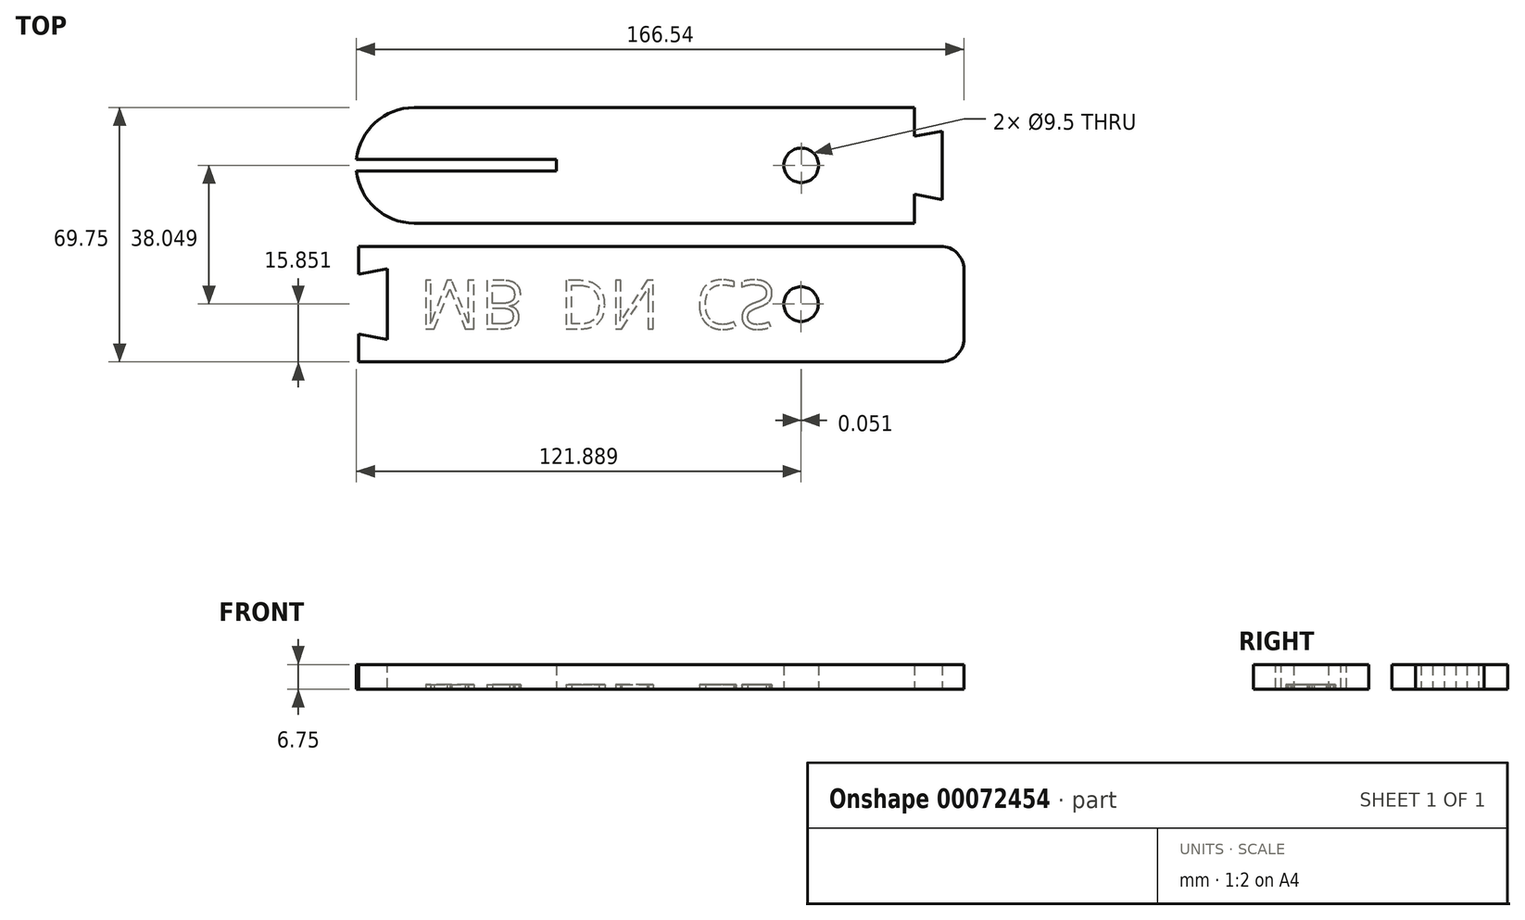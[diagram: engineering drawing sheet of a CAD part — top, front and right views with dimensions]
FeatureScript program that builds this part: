
annotation { "Feature Type Name" : "Feature", "Feature Type Description" : "" }
export const myFeature = defineFeature(function(context is Context, id is Id, definition is map)
    precondition{}
    {
        {
            var Q0;
            Q0=qCreatedBy(makeId("Top.planeOp"),FACE);
            var sketch = newSketch(context, id + "F0", { "sketchPlane" : qUnion([Q0])});
            skLineSegment(sketch, "E0", {"start": v(-148.8, 0) * mm, "end": v(170.22, 0) * mm});
            skLineSegment(sketch, "E1", {"start": v(28.97, 0) * mm, "end": v(28.97, 15.85) * mm});
            skLineSegment(sketch, "E2.MirrorCS", {"start": v(28.97, 0) * mm, "end": v(28.97, -15.85) * mm});
            skLineSegment(sketch, "E3.bottom", {"start": v(-132.95, 15.85) * mm, "end": v(163.87, 15.85) * mm});
            skLineSegment(sketch, "E3.top", {"start": v(-132.95, -15.85) * mm, "end": v(163.87, -15.85) * mm});
            skLineSegment(sketch, "E3.left", {"start": v(-148.8, 0) * mm, "end": v(-148.8, 0) * mm});
            skLineSegment(sketch, "E3.right", {"start": v(170.22, 9.5) * mm, "end": v(170.22, -9.5) * mm});
            skLineSegment(sketch, "E4", {"start": v(-157.4, 0) * mm, "end": v(-157.4, 1.59) * mm});
            skLineSegment(sketch, "E5", {"start": v(-148.8, 25.83) * mm, "end": v(-93.87, 25.83) * mm});
            skLineSegment(sketch, "E6", {"start": v(-148.8, 1.59) * mm, "end": v(-93.87, 1.59) * mm});
            skLineSegment(sketch, "E7.MirrorCS", {"start": v(-148.8, -1.59) * mm, "end": v(-93.87, -1.59) * mm});
            skLineSegment(sketch, "E8", {"start": v(-93.87, -1.59) * mm, "end": v(-93.87, 1.59) * mm});
            skPoint(sketch, "E9.visualSharp", {"position": v(-148.8, 15.85) * mm});
            skArc(sketch, "E9.filletArc", {"start": v(-132.95, 15.85) * mm, "mid": v(-144.16, 11.2) * mm, "end": v(-148.8, 0) * mm});
            skPoint(sketch, "E10.visualSharp", {"position": v(-148.8, -15.85) * mm});
            skArc(sketch, "E10.filletArc", {"start": v(-148.8, 0) * mm, "mid": v(-144.16, -11.2) * mm, "end": v(-132.95, -15.85) * mm});
            skLineSegment(sketch, "E11", {"start": v(170.22, -41.65) * mm, "end": v(125.57, -41.65) * mm});
            skLineSegment(sketch, "E12", {"start": v(170.22, -67.38) * mm, "end": v(-26.78, -67.38) * mm});
            skCircle(sketch, "E13", {"center": v(-26.78, 0) * mm, "radius": 4.75 * mm});
            skCircle(sketch, "E14", {"center": v(125.57, 0) * mm, "radius": 4.75 * mm});
            skLineSegment(sketch, "E15", {"start": v(4.2, 15.85) * mm, "end": v(4.2, 7.92) * mm});
            skPoint(sketch, "E15.endSnap0", {"position": v(28.97, 7.92) * mm});
            skLineSegment(sketch, "E16", {"start": v(4.2, 7.92) * mm, "end": v(11.86, 9.43) * mm});
            skLineSegment(sketch, "E17", {"start": v(11.86, 9.43) * mm, "end": v(11.86, 0) * mm});
            skLineSegment(sketch, "E18.MirrorCS", {"start": v(4.2, -7.92) * mm, "end": v(11.86, -9.43) * mm});
            skLineSegment(sketch, "E19.MirrorCS", {"start": v(11.86, -9.43) * mm, "end": v(11.86, 0) * mm});
            skLineSegment(sketch, "E20.MirrorCS", {"start": v(4.2, -15.85) * mm, "end": v(4.2, -7.92) * mm});
            skPoint(sketch, "E21.visualSharp", {"position": v(170.22, 15.85) * mm});
            skArc(sketch, "E21.filletArc", {"start": v(170.22, 9.5) * mm, "mid": v(168.36, 13.99) * mm, "end": v(163.87, 15.85) * mm});
            skPoint(sketch, "E22.visualSharp", {"position": v(170.22, -15.85) * mm});
            skArc(sketch, "E22.filletArc", {"start": v(163.87, -15.85) * mm, "mid": v(168.36, -13.99) * mm, "end": v(170.22, -9.5) * mm});
            skSolve(sketch);
        }
        {
            var Q0;
            {var subQ3=sQuery(id+"F0.wireOp",EDGE,"E15");Q0=makeQuery(id+"F0.imprint","IMPRINT",FACE,{"disambiguationData":[TD([[makeQuery(id+"F0.imprint","IMPRINT",EDGE,{"derivedFrom":subQ3}),-1.0]])]});}
            var Q1;
            Q1=makeQuery(id+"F0.imprint","IMPRINT",FACE,{"disambiguationData":[TD([[makeQuery(id+"F0.imprint","IMPRINT",EDGE,{"derivedFrom":sQuery(id+"F0.wireOp",EDGE,"E18.MirrorCS")}),1.0]])]});
            extrude(context, id + "F1", {"entities" : qUnion([Q0, Q1]), "depth" : 6.35 * mm});
        }
        {
            var Q0;
            {var subQ1=sQuery(id+"F0.wireOp",EDGE,"E2.MirrorCS");Q0=makeQuery(id+"F0.imprint","IMPRINT",FACE,{"disambiguationData":[TD([[makeQuery(id+"F0.imprint","IMPRINT",EDGE,{"derivedFrom":subQ1}),1.0]])]});}
            var Q1;
            {var subQ1=sQuery(id+"F0.wireOp",EDGE,"E1");Q1=makeQuery(id+"F0.imprint","IMPRINT",FACE,{"disambiguationData":[TD([[makeQuery(id+"F0.imprint","IMPRINT",EDGE,{"derivedFrom":subQ1}),-1.0]])]});}
            var Q2;
            {var subQ0=sQuery(id+"F0.wireOp",EDGE,"E2.MirrorCS");Q2=makeQuery(id+"F0.imprint","IMPRINT",FACE,{"disambiguationData":[TD([[makeQuery(id+"F0.imprint","IMPRINT",EDGE,{"derivedFrom":subQ0}),-1.0]])]});}
            var Q3;
            {var subQ2=sQuery(id+"F0.wireOp",EDGE,"E1");Q3=makeQuery(id+"F0.imprint","IMPRINT",FACE,{"disambiguationData":[TD([[makeQuery(id+"F0.imprint","IMPRINT",EDGE,{"derivedFrom":subQ2}),1.0]])]});}
            extrude(context, id + "F2", {"entities" : qUnion([Q0, Q1, Q2, Q3]), "depth" : 6.35 * mm});
        }
        {
            var Q0;
            Q0=makeQuery(id+"F2.opExtrude","SWEPT_BODY",BODY,{"disambiguationData":[OSD([sQuery(id+"F0.wireOp",EDGE,"E3.bottom"),sQuery(id+"F0.wireOp",EDGE,"E3.top"),sQuery(id+"F0.wireOp",EDGE,"E3.right"),sQuery(id+"F0.wireOp",EDGE,"E14"),sQuery(id+"F0.wireOp",EDGE,"E15"),sQuery(id+"F0.wireOp",EDGE,"E16"),sQuery(id+"F0.wireOp",EDGE,"E17"),sQuery(id+"F0.wireOp",EDGE,"E18.MirrorCS"),sQuery(id+"F0.wireOp",EDGE,"E19.MirrorCS"),sQuery(id+"F0.wireOp",EDGE,"E20.MirrorCS"),sQuery(id+"F0.wireOp",EDGE,"E21.filletArc"),sQuery(id+"F0.wireOp",EDGE,"E22.filletArc")])]});
            var Q1;
            Q1=sQuery(id+"F0.wireOp",EDGE,"E2.MirrorCS");
            transform(context, id + "F3", {"entities" : qUnion([Q0]), "transformType" : TransformType.TRANSLATION_ENTITY, "oppositeDirectionEntity" : false, "transformLine" : qUnion([Q1]), "makeCopy" : false});
        }
        {
            var Q0;
            Q0=makeQuery(id+"F2.opExtrude","SWEPT_BODY",BODY,{"disambiguationData":[OSD([sQuery(id+"F0.wireOp",EDGE,"E3.bottom"),sQuery(id+"F0.wireOp",EDGE,"E3.top"),sQuery(id+"F0.wireOp",EDGE,"E3.right"),sQuery(id+"F0.wireOp",EDGE,"E14"),sQuery(id+"F0.wireOp",EDGE,"E15"),sQuery(id+"F0.wireOp",EDGE,"E16"),sQuery(id+"F0.wireOp",EDGE,"E17"),sQuery(id+"F0.wireOp",EDGE,"E18.MirrorCS"),sQuery(id+"F0.wireOp",EDGE,"E19.MirrorCS"),sQuery(id+"F0.wireOp",EDGE,"E20.MirrorCS"),sQuery(id+"F0.wireOp",EDGE,"E21.filletArc"),sQuery(id+"F0.wireOp",EDGE,"E22.filletArc")])]});
            var Q1;
            Q1=sQuery(id+"F0.wireOp",EDGE,"E2.MirrorCS");
            transform(context, id + "F4", {"entities" : qUnion([Q0]), "transformType" : TransformType.TRANSLATION_ENTITY, "oppositeDirectionEntity" : false, "transformLine" : qUnion([Q1]), "makeCopy" : false});
        }
        {
            var Q0;
            Q0=makeQuery(id+"F2.opExtrude","SWEPT_BODY",BODY,{"disambiguationData":[OSD([sQuery(id+"F0.wireOp",EDGE,"E3.bottom"),sQuery(id+"F0.wireOp",EDGE,"E3.top"),sQuery(id+"F0.wireOp",EDGE,"E3.right"),sQuery(id+"F0.wireOp",EDGE,"E14"),sQuery(id+"F0.wireOp",EDGE,"E15"),sQuery(id+"F0.wireOp",EDGE,"E16"),sQuery(id+"F0.wireOp",EDGE,"E17"),sQuery(id+"F0.wireOp",EDGE,"E18.MirrorCS"),sQuery(id+"F0.wireOp",EDGE,"E19.MirrorCS"),sQuery(id+"F0.wireOp",EDGE,"E20.MirrorCS"),sQuery(id+"F0.wireOp",EDGE,"E21.filletArc"),sQuery(id+"F0.wireOp",EDGE,"E22.filletArc")])]});
            transform(context, id + "F5", {"entities" : qUnion([Q0]), "transformType" : TransformType.TRANSLATION_3D, "dx" : -152.4 * mm, "dy" : -6.35 * mm, "dz" : 0 * mm, "makeCopy" : false});
        }
        {
            var Q0;
            Q0=makeQuery(id+"F2.opExtrude","CAP_FACE",FACE,{"disambiguationData":[OSD([sQuery(id+"F0.wireOp",EDGE,"E3.bottom"),sQuery(id+"F0.wireOp",EDGE,"E3.top"),sQuery(id+"F0.wireOp",EDGE,"E3.right"),sQuery(id+"F0.wireOp",EDGE,"E14"),sQuery(id+"F0.wireOp",EDGE,"E15"),sQuery(id+"F0.wireOp",EDGE,"E16"),sQuery(id+"F0.wireOp",EDGE,"E17"),sQuery(id+"F0.wireOp",EDGE,"E18.MirrorCS"),sQuery(id+"F0.wireOp",EDGE,"E19.MirrorCS"),sQuery(id+"F0.wireOp",EDGE,"E20.MirrorCS"),sQuery(id+"F0.wireOp",EDGE,"E21.filletArc"),sQuery(id+"F0.wireOp",EDGE,"E22.filletArc")])],"isStart":true});
            var sketch = newSketch(context, id + "F6", { "sketchPlane" : qUnion([Q0])});
            skText(sketch, "E23", { "text": "MB  DN  CS", "fontName": "OpenSans-Regular.ttf"});
            const initialGuessF6  = {"E23": [-0.13154, 0.03158, 1, 0, 0.01338]};
            skSetInitialGuess(sketch, initialGuessF6);
            skSolve(sketch);
        }
        {
            var Q0;
            Q0 = qSketchRegion(id + "F6", true);
            extrude(context, id + "F7", {"entities" : qUnion([Q0]), "operationType" : NewBodyOperationType.REMOVE, "oppositeDirection" : true, "depth" : 1.25 * mm});
        }
        {
            var Q0;
            Q0=makeQuery(id+"F1.opExtrude","CAP_FACE",FACE,{"disambiguationData":[OSD([sQuery(id+"F0.wireOp",EDGE,"E3.bottom"),sQuery(id+"F0.wireOp",EDGE,"E3.top"),sQuery(id+"F0.wireOp",EDGE,"E6"),sQuery(id+"F0.wireOp",EDGE,"E7.MirrorCS"),sQuery(id+"F0.wireOp",EDGE,"E8"),sQuery(id+"F0.wireOp",EDGE,"E9.filletArc"),sQuery(id+"F0.wireOp",EDGE,"E10.filletArc"),sQuery(id+"F0.wireOp",EDGE,"E13"),sQuery(id+"F0.wireOp",EDGE,"E15"),sQuery(id+"F0.wireOp",EDGE,"E16"),sQuery(id+"F0.wireOp",EDGE,"E17"),sQuery(id+"F0.wireOp",EDGE,"E18.MirrorCS"),sQuery(id+"F0.wireOp",EDGE,"E19.MirrorCS"),sQuery(id+"F0.wireOp",EDGE,"E20.MirrorCS")])],"isStart":false});
            var Q1;
            Q1=makeQuery(id+"F2.opExtrude","CAP_FACE",FACE,{"disambiguationData":[OSD([sQuery(id+"F0.wireOp",EDGE,"E3.bottom"),sQuery(id+"F0.wireOp",EDGE,"E3.top"),sQuery(id+"F0.wireOp",EDGE,"E3.right"),sQuery(id+"F0.wireOp",EDGE,"E14"),sQuery(id+"F0.wireOp",EDGE,"E15"),sQuery(id+"F0.wireOp",EDGE,"E16"),sQuery(id+"F0.wireOp",EDGE,"E17"),sQuery(id+"F0.wireOp",EDGE,"E18.MirrorCS"),sQuery(id+"F0.wireOp",EDGE,"E19.MirrorCS"),sQuery(id+"F0.wireOp",EDGE,"E20.MirrorCS"),sQuery(id+"F0.wireOp",EDGE,"E21.filletArc"),sQuery(id+"F0.wireOp",EDGE,"E22.filletArc")])],"isStart":false});
            extrude(context, id + "F8", {"entities" : qUnion([Q0, Q1]), "operationType" : NewBodyOperationType.ADD, "depth" : 0.4 * mm});
        }
        {
            var Q0;
            Q0=makeQuery(id+"F8.opExtrude","CAP_FACE",FACE,{"disambiguationData":[OSD([sQuery(id+"F0.wireOp",EDGE,"E3.bottom"),sQuery(id+"F0.wireOp",EDGE,"E3.top"),sQuery(id+"F0.wireOp",EDGE,"E3.right"),sQuery(id+"F0.wireOp",EDGE,"E14"),sQuery(id+"F0.wireOp",EDGE,"E15"),sQuery(id+"F0.wireOp",EDGE,"E16"),sQuery(id+"F0.wireOp",EDGE,"E17"),sQuery(id+"F0.wireOp",EDGE,"E18.MirrorCS"),sQuery(id+"F0.wireOp",EDGE,"E19.MirrorCS"),sQuery(id+"F0.wireOp",EDGE,"E20.MirrorCS"),sQuery(id+"F0.wireOp",EDGE,"E21.filletArc"),sQuery(id+"F0.wireOp",EDGE,"E22.filletArc")])],"isStart":false});
            var sketch = newSketch(context, id + "F9", { "sketchPlane" : qUnion([Q0])});
            skLineSegment(sketch, "E24", {"start": v(-148.2, -30.12) * mm, "end": v(-140.54, -28.62) * mm});
            skLineSegment(sketch, "E25", {"start": v(-140.54, -28.62) * mm, "end": v(-140.54, -47.48) * mm});
            skLineSegment(sketch, "E26", {"start": v(-140.54, -47.48) * mm, "end": v(-148.2, -45.97) * mm});
            skLineSegment(sketch, "E27.0", {"start": v(-148.2, -29.87) * mm, "end": v(-140.29, -28.32) * mm});
            skLineSegment(sketch, "E28.0", {"start": v(-140.29, -28.32) * mm, "end": v(-140.29, -47.78) * mm});
            skLineSegment(sketch, "E29.0", {"start": v(-140.29, -47.78) * mm, "end": v(-148.2, -46.23) * mm});
            skLineSegment(sketch, "E30", {"start": v(-148.2, -45.97) * mm, "end": v(-148.2, -46.23) * mm});
            skLineSegment(sketch, "E31", {"start": v(-148.2, -30.12) * mm, "end": v(-148.2, -29.87) * mm});
            skSolve(sketch);
        }
        {
            var Q0;
            Q0 = qSketchRegion(id + "F9", true);
            extrude(context, id + "F10", {"entities" : qUnion([Q0]), "operationType" : NewBodyOperationType.REMOVE, "endBound" : BoundingType.UP_TO_NEXT, "oppositeDirection" : true, "depth" : 25 * mm});
        }
    });
